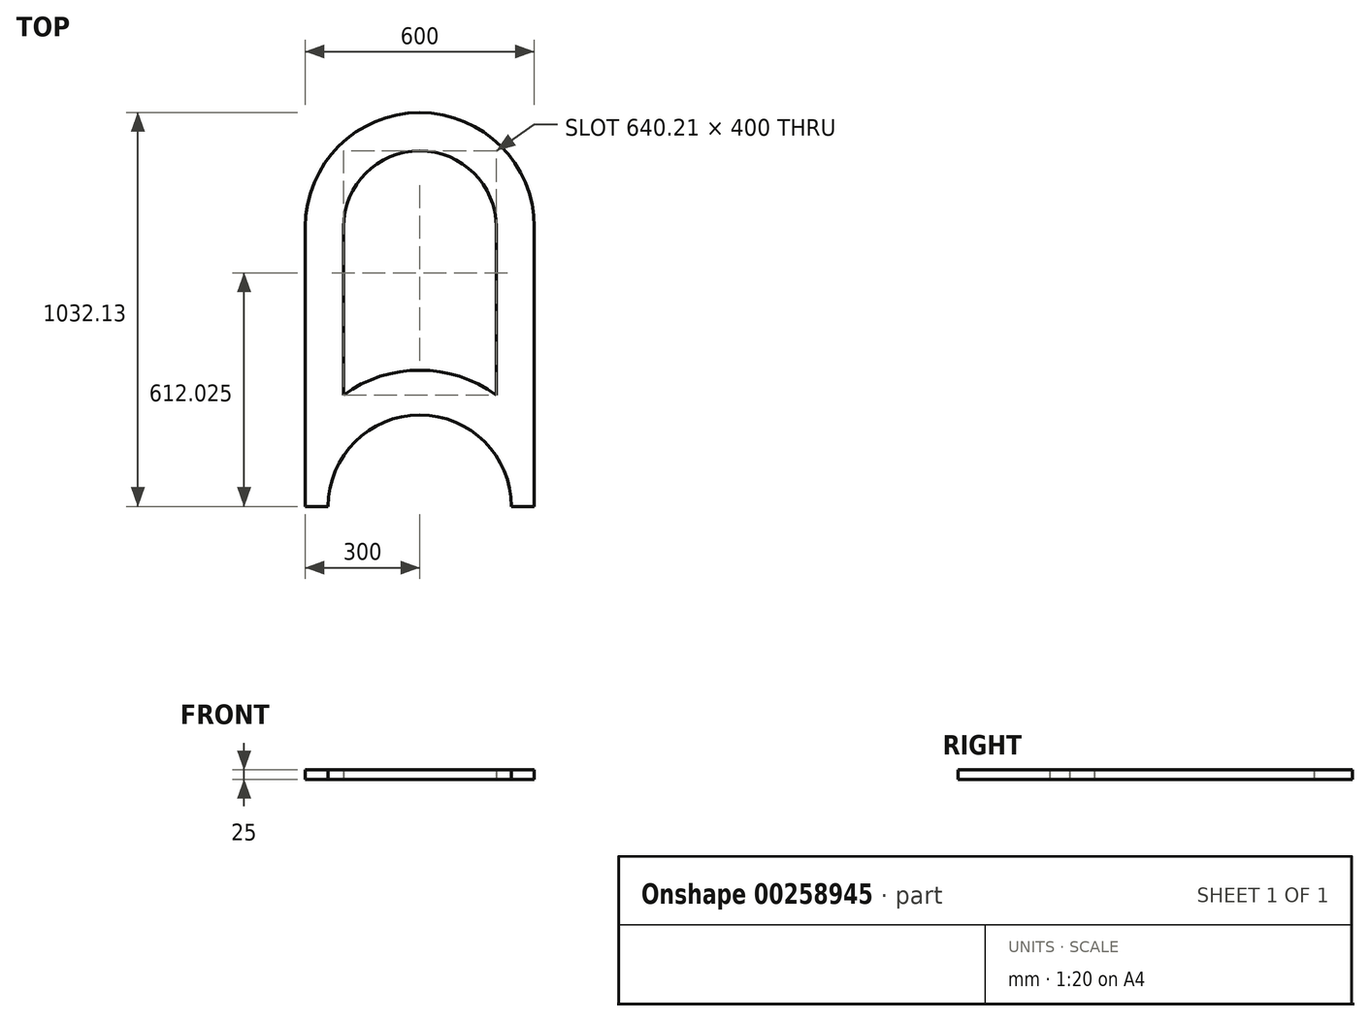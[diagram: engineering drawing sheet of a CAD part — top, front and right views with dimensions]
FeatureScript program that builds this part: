
annotation { "Feature Type Name" : "Feature", "Feature Type Description" : "" }
export const myFeature = defineFeature(function(context is Context, id is Id, definition is map)
    precondition{}
    {
        {
            var Q0;
            Q0=qCreatedBy(makeId("Top.planeOp"),FACE);
            var sketch = newSketch(context, id + "F0", { "sketchPlane" : qUnion([Q0])});
            skLineSegment(sketch, "E0", {"start": v(-300, -291.92) * mm, "end": v(-300, 440.21) * mm});
            skLineSegment(sketch, "E1", {"start": v(-300, -291.92) * mm, "end": v(-240, -291.92) * mm});
            skLineSegment(sketch, "E2", {"start": v(240, -291.92) * mm, "end": v(300, -291.92) * mm});
            skLineSegment(sketch, "E3", {"start": v(300, -291.92) * mm, "end": v(300, 440.21) * mm});
            skArc(sketch, "E4", {"start": v(300, 440.21) * mm, "mid": v(0, 740.21) * mm, "end": v(-300, 440.21) * mm});
            skPoint(sketch, "E5.endSnap0", {"position": v(0, 740.21) * mm});
            skArc(sketch, "E6", {"start": v(240, -291.92) * mm, "mid": v(0, -51.92) * mm, "end": v(-240, -291.92) * mm});
            skLineSegment(sketch, "E7", {"start": v(-200, 0) * mm, "end": v(-200, 440.21) * mm});
            skLineSegment(sketch, "E8", {"start": v(200, 440.21) * mm, "end": v(200, 0) * mm});
            skArc(sketch, "E9", {"start": v(200, 440.21) * mm, "mid": v(0, 640.21) * mm, "end": v(-200, 440.21) * mm});
            skPoint(sketch, "E10.endSnap0", {"position": v(0, 640.21) * mm});
            skArc(sketch, "E11", {"start": v(200, 0) * mm, "mid": v(0, 65.05) * mm, "end": v(-200, 0) * mm});
            skSolve(sketch);
        }
        {
            var Q0;
            Q0 = qSketchRegion(id + "F0", true);
            extrude(context, id + "F1", {"entities" : qUnion([Q0]), "depth" : 25 * mm});
        }
    });
